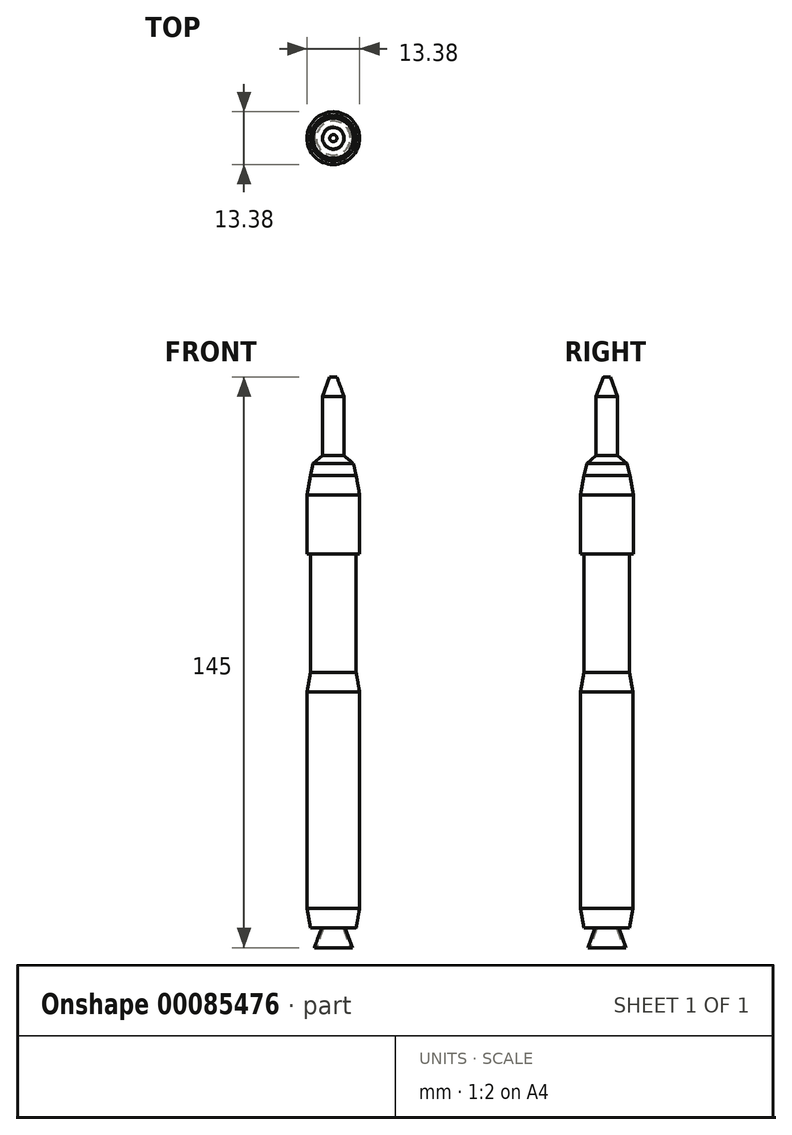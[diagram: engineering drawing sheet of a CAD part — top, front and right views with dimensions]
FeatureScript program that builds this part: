
annotation { "Feature Type Name" : "Feature", "Feature Type Description" : "" }
export const myFeature = defineFeature(function(context is Context, id is Id, definition is map)
    precondition{}
    {
        {
            var Q0;
            Q0=qCreatedBy(makeId("Top.planeOp"),FACE);
            var sketch = newSketch(context, id + "F0", { "sketchPlane" : qUnion([Q0])});
            skCircle(sketch, "E0", {"center": v(0, 0) * mm, "radius": 6.67 * mm});
            skSolve(sketch);
        }
        {
            var Q0;
            Q0=makeQuery(id+"F0.imprint","IMPRINT",FACE,{"disambiguationData":[TD([[makeQuery(id+"F0.imprint","IMPRINT",EDGE,{"derivedFrom":sQuery(id+"F0.wireOp",EDGE,"E0")}),1.0]])]});
            extrude(context, id + "F1", {"entities" : qUnion([Q0]), "depth" : 5 * mm, "hasSecondDirection" : true, "secondDirectionOppositeDirection" : true, "secondDirectionDepth" : 50 * mm});
        }
        {
            var Q0;
            Q0=makeQuery(id+"F1.opExtrude","CAP_FACE",FACE,{"disambiguationData":[OSD([sQuery(id+"F0.wireOp",EDGE,"E0")])],"isStart":false});
            extrude(context, id + "F2", {"entities" : qUnion([Q0]), "operationType" : NewBodyOperationType.ADD, "depth" : 5 * mm, "hasDraft" : true, "draftAngle" : 10 * degree, "draftPullDirection" : true});
        }
        {
            var Q0;
            Q0=makeQuery(id+"F1.opExtrude","CAP_FACE",FACE,{"disambiguationData":[OSD([sQuery(id+"F0.wireOp",EDGE,"E0")])],"isStart":true});
            extrude(context, id + "F3", {"entities" : qUnion([Q0]), "operationType" : NewBodyOperationType.ADD, "depth" : 5 * mm, "hasDraft" : true, "draftAngle" : 10 * degree, "draftPullDirection" : true});
        }
        {
            var Q0;
            Q0=makeQuery(id+"F3.opExtrude","CAP_FACE",FACE,{"disambiguationData":[OSD([sQuery(id+"F0.wireOp",EDGE,"E0")])],"isStart":false});
            var sketch = newSketch(context, id + "F4", { "sketchPlane" : qUnion([Q0])});
            skCircle(sketch, "E1", {"center": v(0, 0) * mm, "radius": 3.02 * mm});
            skSolve(sketch);
        }
        {
            var Q0;
            Q0 = qSketchRegion(id + "F4", true);
            extrude(context, id + "F5", {"entities" : qUnion([Q0]), "operationType" : NewBodyOperationType.ADD, "depth" : 5 * mm, "hasDraft" : true, "draftAngle" : 20 * degree});
        }
        {
            var Q0;
            Q0=makeQuery(id+"F5.opExtrude","CAP_FACE",FACE,{"disambiguationData":[OSD([sQuery(id+"F4.wireOp",EDGE,"E1")])],"isStart":false});
            var sketch = newSketch(context, id + "F6", { "sketchPlane" : qUnion([Q0])});
            skCircle(sketch, "E2", {"center": v(0, 0) * mm, "radius": 4.3 * mm});
            skSolve(sketch);
        }
        {
            var Q0;
            Q0 = qSketchRegion(id + "F6", true);
            extrude(context, id + "F7", {"entities" : qUnion([Q0]), "operationType" : NewBodyOperationType.REMOVE, "oppositeDirection" : true, "depth" : 5 * mm, "hasDraft" : true, "draftAngle" : 20 * degree, "draftPullDirection" : true});
        }
        {
            var Q0;
            Q0=makeQuery(id+"F2.opExtrude","CAP_FACE",FACE,{"disambiguationData":[OSD([sQuery(id+"F0.wireOp",EDGE,"E0")])],"isStart":false});
            extrude(context, id + "F8", {"entities" : qUnion([Q0]), "operationType" : NewBodyOperationType.ADD, "depth" : 30 * mm});
        }
        {
            var Q0;
            Q0=makeQuery(id+"F8.opExtrude","CAP_FACE",FACE,{"disambiguationData":[OSD([sQuery(id+"F0.wireOp",EDGE,"E0")])],"isStart":false});
            var sketch = newSketch(context, id + "F9", { "sketchPlane" : qUnion([Q0])});
            skCircle(sketch, "E3", {"center": v(0, 0) * mm, "radius": 6.7 * mm});
            skSolve(sketch);
        }
        {
            var Q0;
            Q0 = qSketchRegion(id + "F9", true);
            extrude(context, id + "F10", {"entities" : qUnion([Q0]), "operationType" : NewBodyOperationType.ADD, "depth" : 15 * mm});
        }
        {
            var Q0;
            Q0=makeQuery(id+"F10.opExtrude","CAP_FACE",FACE,{"disambiguationData":[OSD([sQuery(id+"F9.wireOp",EDGE,"E3")])],"isStart":false});
            extrude(context, id + "F11", {"entities" : qUnion([Q0]), "operationType" : NewBodyOperationType.ADD, "depth" : 5 * mm, "hasDraft" : true, "draftAngle" : 10 * degree, "draftPullDirection" : true});
        }
        {
            var Q0;
            Q0=makeQuery(id+"F11.opExtrude","CAP_FACE",FACE,{"disambiguationData":[OSD([sQuery(id+"F9.wireOp",EDGE,"E3")])],"isStart":false});
            extrude(context, id + "F12", {"entities" : qUnion([Q0]), "operationType" : NewBodyOperationType.ADD, "depth" : 3 * mm, "hasDraft" : true, "draftAngle" : 13 * degree, "draftPullDirection" : true});
        }
        {
            var Q0;
            Q0=makeQuery(id+"F12.opExtrude","CAP_FACE",FACE,{"disambiguationData":[OSD([sQuery(id+"F9.wireOp",EDGE,"E3")])],"isStart":false});
            extrude(context, id + "F13", {"entities" : qUnion([Q0]), "operationType" : NewBodyOperationType.ADD, "depth" : 2 * mm, "hasDraft" : true, "draftAngle" : 50 * degree, "draftPullDirection" : true});
        }
        {
            var Q0;
            Q0=makeQuery(id+"F13.opExtrude","CAP_FACE",FACE,{"disambiguationData":[OSD([sQuery(id+"F9.wireOp",EDGE,"E3")])],"isStart":false});
            extrude(context, id + "F14", {"entities" : qUnion([Q0]), "operationType" : NewBodyOperationType.ADD, "depth" : 15 * mm});
        }
        {
            var Q0;
            Q0=makeQuery(id+"F14.opExtrude","CAP_FACE",FACE,{"disambiguationData":[OSD([sQuery(id+"F9.wireOp",EDGE,"E3")])],"isStart":false});
            extrude(context, id + "F15", {"entities" : qUnion([Q0]), "operationType" : NewBodyOperationType.ADD, "depth" : 5 * mm, "hasDraft" : true, "draftAngle" : 20 * degree, "draftPullDirection" : true});
        }
    });
